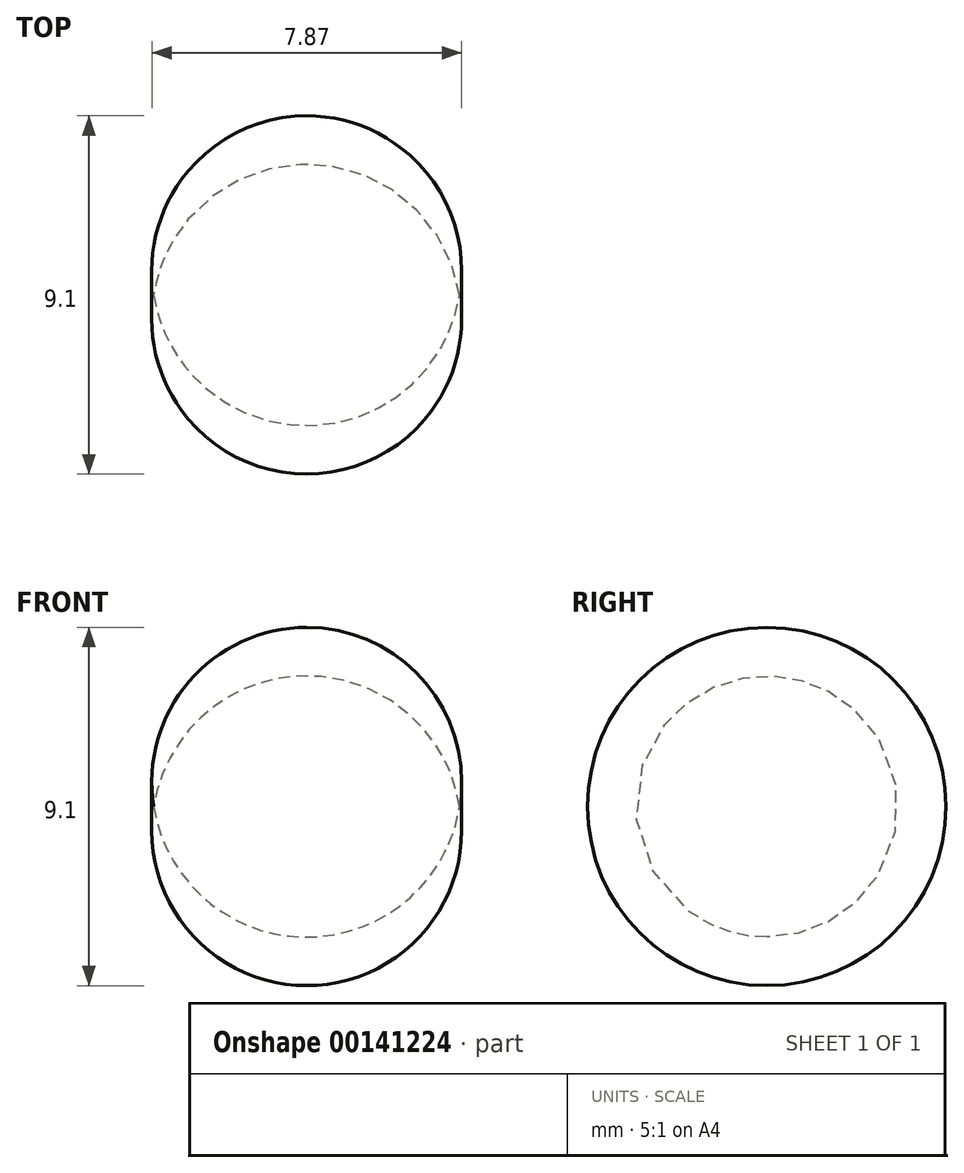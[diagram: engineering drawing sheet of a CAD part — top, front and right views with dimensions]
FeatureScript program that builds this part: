
annotation { "Feature Type Name" : "Feature", "Feature Type Description" : "" }
export const myFeature = defineFeature(function(context is Context, id is Id, definition is map)
    precondition{}
    {
        {
            var Q0;
            Q0=qCreatedBy(makeId("Front.planeOp"),FACE);
            var sketch = newSketch(context, id + "F0", { "sketchPlane" : qUnion([Q0])});
            skLineSegment(sketch, "E0", {"start": v(-64.79, 45.67) * mm, "end": v(-57.01, 45.67) * mm});
            skArc(sketch, "E1", {"start": v(-57.01, 45.67) * mm, "mid": v(-60.9, 49) * mm, "end": v(-64.79, 45.67) * mm});
            skSolve(sketch);
        }
        {
            var Q0;
            Q0=makeQuery(id+"F0.imprint","IMPRINT",FACE,{"disambiguationData":[TD([[makeQuery(id+"F0.imprint","IMPRINT",EDGE,{"derivedFrom":sQuery(id+"F0.wireOp",EDGE,"E0")}),1.0]])]});
            var Q1;
            Q1=sQuery(id+"F0.wireOp",EDGE,"E0");
            revolve(context, id + "F1", {"entities" : qUnion([Q0]), "axis" : qUnion([Q1]), "revolveType" : RevolveType.FULL});
        }
    });
